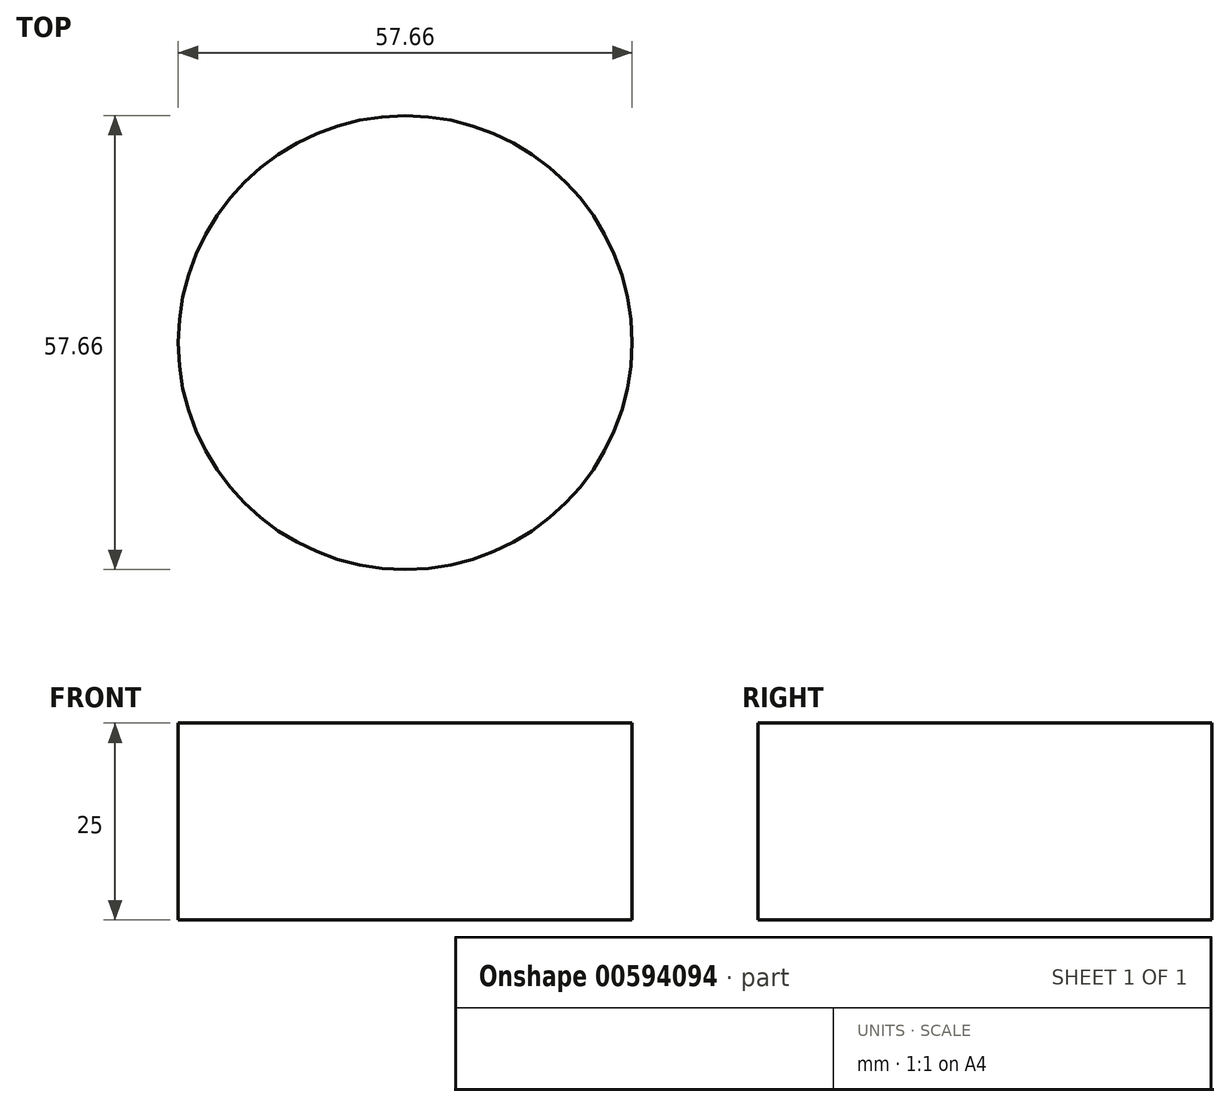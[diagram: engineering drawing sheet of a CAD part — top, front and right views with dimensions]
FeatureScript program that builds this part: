
annotation { "Feature Type Name" : "Feature", "Feature Type Description" : "" }
export const myFeature = defineFeature(function(context is Context, id is Id, definition is map)
    precondition{}
    {
        {
            var Q0;
            Q0=qCreatedBy(makeId("Top.planeOp"),FACE);
            var sketch = newSketch(context, id + "F0", { "sketchPlane" : qUnion([Q0])});
            skCircle(sketch, "E0", {"center": v(0, 0) * mm, "radius": 28.83 * mm});
            skSolve(sketch);
        }
        {
            var Q0;
            Q0 = qSketchRegion(id + "F0", true);
            extrude(context, id + "F1", {"entities" : qUnion([Q0]), "depth" : 25 * mm, "offsetDistance" : 25 * mm});
        }
    });
